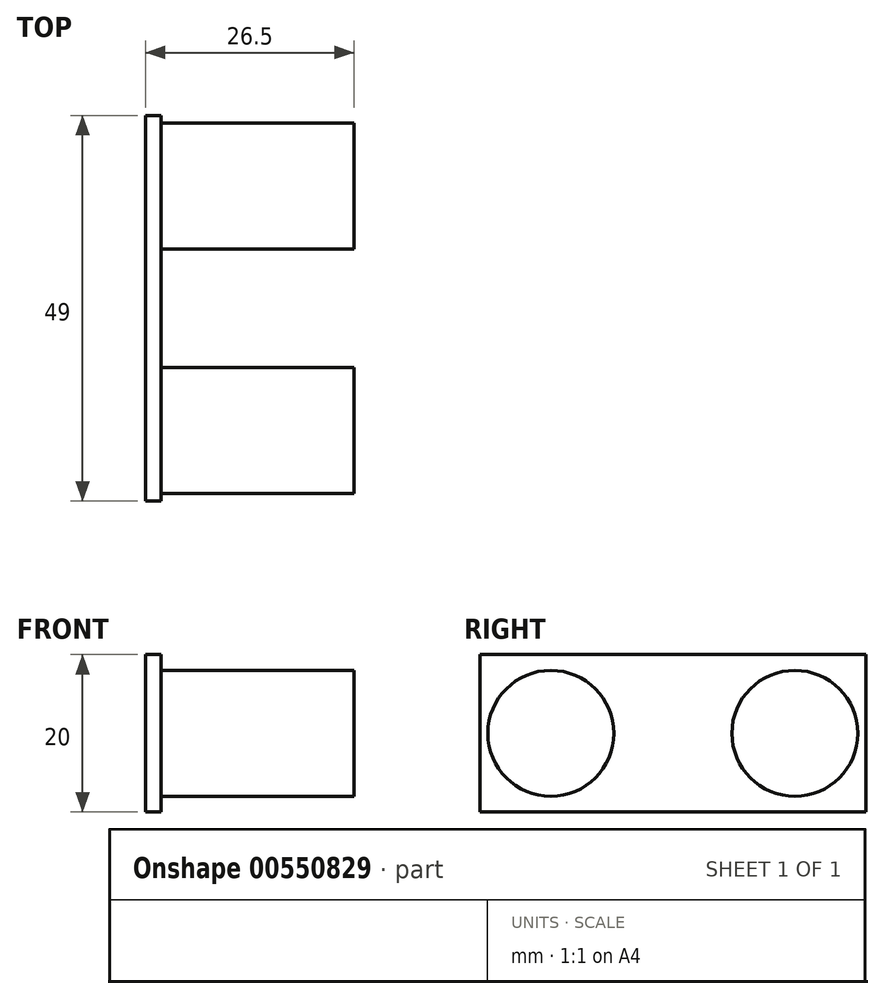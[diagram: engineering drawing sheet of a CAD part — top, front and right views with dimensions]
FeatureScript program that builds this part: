
annotation { "Feature Type Name" : "Feature", "Feature Type Description" : "" }
export const myFeature = defineFeature(function(context is Context, id is Id, definition is map)
    precondition{}
    {
        {
            var Q0;
            Q0=qCreatedBy(makeId("Right.planeOp"),FACE);
            var sketch = newSketch(context, id + "F0", { "sketchPlane" : qUnion([Q0])});
            skLineSegment(sketch, "E0", {"start": v(-15.5, 0) * mm, "end": v(15.5, 0) * mm, "construction": true});
            skCircle(sketch, "E1", {"center": v(-15.5, 0) * mm, "radius": 8 * mm});
            skCircle(sketch, "E2", {"center": v(15.5, 0) * mm, "radius": 8 * mm});
            skSolve(sketch);
        }
        {
            var Q0;
            Q0=makeQuery(id+"F0.imprint","IMPRINT",FACE,{"disambiguationData":[TD([[makeQuery(id+"F0.imprint","IMPRINT",EDGE,{"derivedFrom":sQuery(id+"F0.wireOp",EDGE,"E1")}),1.0]])]});
            var Q1;
            Q1=makeQuery(id+"F0.imprint","IMPRINT",FACE,{"disambiguationData":[TD([[makeQuery(id+"F0.imprint","IMPRINT",EDGE,{"derivedFrom":sQuery(id+"F0.wireOp",EDGE,"E2")}),1.0]])]});
            extrude(context, id + "F1", {"entities" : qUnion([Q0, Q1]), "depth" : 24.5 * mm, "offsetDistance" : 25 * mm});
        }
        {
            var Q0;
            Q0=qCreatedBy(makeId("Right.planeOp"),FACE);
            var sketch = newSketch(context, id + "F2", { "sketchPlane" : qUnion([Q0])});
            skLineSegment(sketch, "E3.bottom", {"start": v(-24.5, 10) * mm, "end": v(24.5, 10) * mm});
            skLineSegment(sketch, "E3.top", {"start": v(-24.5, -10) * mm, "end": v(24.5, -10) * mm});
            skLineSegment(sketch, "E3.left", {"start": v(-24.5, 10) * mm, "end": v(-24.5, -10) * mm});
            skLineSegment(sketch, "E3.right", {"start": v(24.5, 10) * mm, "end": v(24.5, -10) * mm});
            skSolve(sketch);
        }
        {
            var Q0;
            Q0=makeQuery(id+"F2.imprint","IMPRINT",FACE,{"disambiguationData":[TD([[makeQuery(id+"F2.imprint","IMPRINT",EDGE,{"derivedFrom":sQuery(id+"F2.wireOp",EDGE,"E3.bottom")}),-1.0]])]});
            extrude(context, id + "F3", {"entities" : qUnion([Q0]), "oppositeDirection" : true, "depth" : 2 * mm, "offsetDistance" : 25 * mm});
        }
    });
